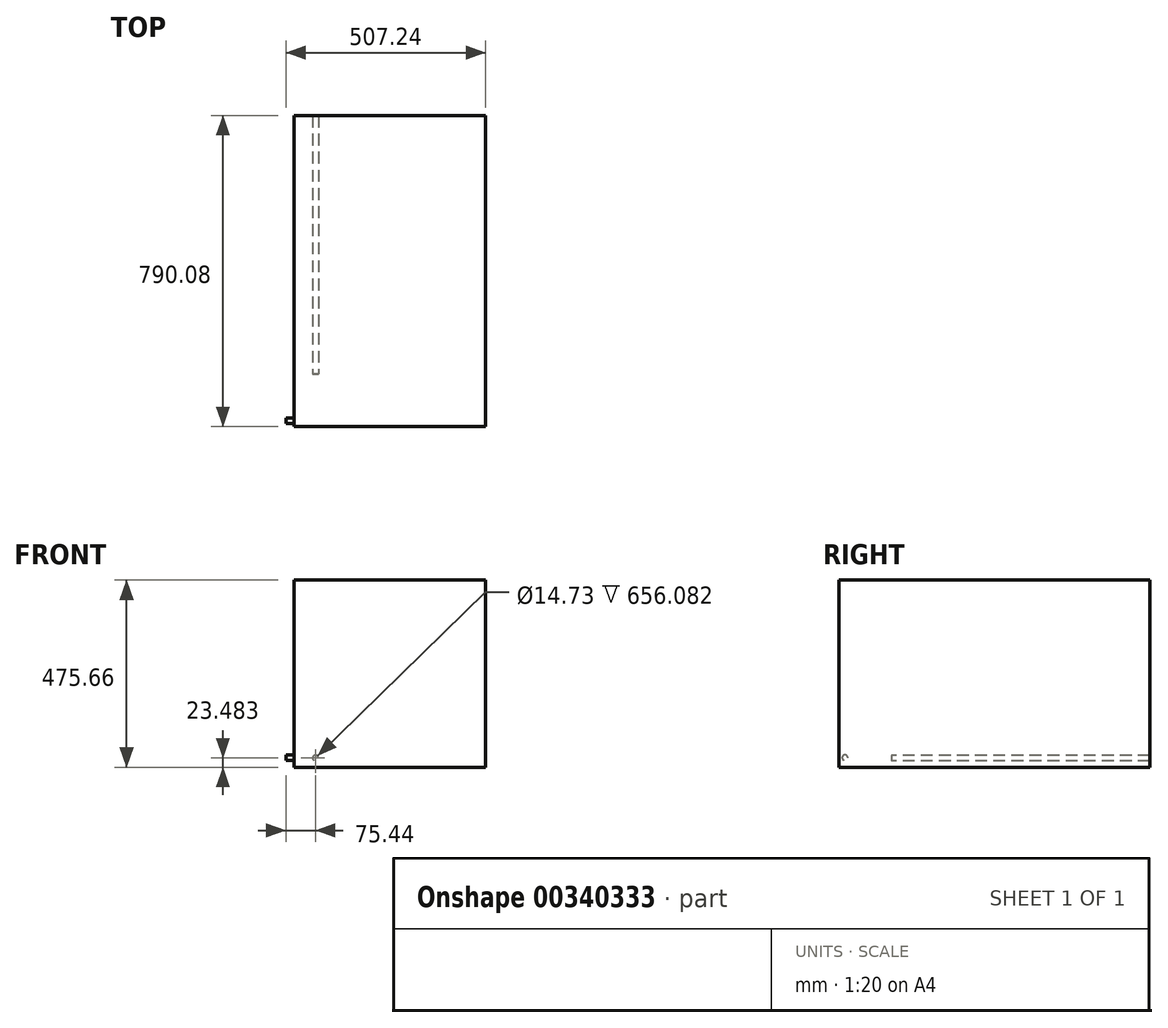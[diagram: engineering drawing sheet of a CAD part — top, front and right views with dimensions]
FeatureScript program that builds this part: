
annotation { "Feature Type Name" : "Feature", "Feature Type Description" : "" }
export const myFeature = defineFeature(function(context is Context, id is Id, definition is map)
    precondition{}
    {
        {
            var Q0;
            Q0=qCreatedBy(makeId("Right.planeOp"),FACE);
            var sketch = newSketch(context, id + "F0", { "sketchPlane" : qUnion([Q0])});
            skLineSegment(sketch, "E0", {"start": v(-46.44, -18.34) * mm, "end": v(36, -18.34) * mm});
            skLineSegment(sketch, "E1", {"start": v(-46.44, 25.52) * mm, "end": v(36, 25.52) * mm});
            skLineSegment(sketch, "E2", {"start": v(-46.44, 25.52) * mm, "end": v(-46.44, -18.34) * mm});
            skLineSegment(sketch, "E3", {"start": v(36, 25.52) * mm, "end": v(36, -18.34) * mm});
            skSolve(sketch);
        }
        {
            var Q0;
            Q0 = qSketchRegion(id + "F0", true);
            extrude(context, id + "F1", {"entities" : qUnion([Q0]), "depth" : 431.8 * mm});
        }
        {
            var Q0;
            Q0=makeQuery(id+"F1.opExtrude","CAP_FACE",FACE,{"disambiguationData":[OSD([sQuery(id+"F0.wireOp",EDGE,"E0"),sQuery(id+"F0.wireOp",EDGE,"E1"),sQuery(id+"F0.wireOp",EDGE,"E2"),sQuery(id+"F0.wireOp",EDGE,"E3")])],"isStart":true});
            extrude(context, id + "F2", {"entities" : qUnion([Q0]), "operationType" : NewBodyOperationType.ADD, "depth" : 54.86 * mm});
        }
        {
            var Q0;
            Q0=makeQuery(id+"F2.opExtrude","CAP_FACE",FACE,{"disambiguationData":[OSD([sQuery(id+"F0.wireOp",EDGE,"E0"),sQuery(id+"F0.wireOp",EDGE,"E1"),sQuery(id+"F0.wireOp",EDGE,"E2"),sQuery(id+"F0.wireOp",EDGE,"E3")])],"isStart":false});
            var sketch = newSketch(context, id + "F3", { "sketchPlane" : qUnion([Q0])});
            skCircle(sketch, "E4", {"center": v(31.25, 5.96) * mm, "radius": 7.09 * mm});
            skSolve(sketch);
        }
        {
            var Q0;
            Q0=makeQuery(id+"F3.imprint","IMPRINT",FACE,{"disambiguationData":[TD([[makeQuery(id+"F3.imprint","IMPRINT",EDGE,{"derivedFrom":sQuery(id+"F3.wireOp",EDGE,"E4")}),1.0]])]});
            extrude(context, id + "F4", {"entities" : qUnion([Q0]), "operationType" : NewBodyOperationType.ADD, "depth" : 20.57 * mm});
        }
        {
            var Q0;
            {var subQ0=sQuery(id+"F0.wireOp",EDGE,"E3");Q0=makeQuery(id+"F2.boolean.opBoolean","MERGE",FACE,{"derivedFrom":[makeQuery(id+"F1.opExtrude","SWEPT_FACE",FACE,{"disambiguationData":[OSD([subQ0])]}),makeQuery(id+"F2.opExtrude","SWEPT_FACE",FACE,{"disambiguationData":[OSD([subQ0])]})]});}
            var sketch = newSketch(context, id + "F5", { "sketchPlane" : qUnion([Q0])});
            skCircle(sketch, "E5", {"center": v(0, 5.14) * mm, "radius": 7.36 * mm});
            skSolve(sketch);
        }
        {
            var Q0;
            Q0=makeQuery(id+"F5.imprint","IMPRINT",FACE,{"disambiguationData":[TD([[makeQuery(id+"F5.imprint","IMPRINT",EDGE,{"derivedFrom":sQuery(id+"F5.wireOp",EDGE,"E5")}),1.0]])]});
            extrude(context, id + "F6", {"entities" : qUnion([Q0]), "operationType" : NewBodyOperationType.ADD, "depth" : 14.48 * mm});
        }
        {
            var Q0;
            {var subQ0=sQuery(id+"F0.wireOp",EDGE,"E3");Q0=makeQuery(id+"F2.boolean.opBoolean","MERGE",FACE,{"derivedFrom":[makeQuery(id+"F1.opExtrude","SWEPT_FACE",FACE,{"disambiguationData":[OSD([subQ0])]}),makeQuery(id+"F2.opExtrude","SWEPT_FACE",FACE,{"disambiguationData":[OSD([subQ0])]})]});}
            extrude(context, id + "F7", {"entities" : qUnion([Q0]), "operationType" : NewBodyOperationType.ADD, "depth" : 34.54 * mm});
        }
        {
            var Q0;
            Q0=makeQuery(id+"F6.opExtrude","CAP_FACE",FACE,{"disambiguationData":[OSD([sQuery(id+"F5.wireOp",EDGE,"E5")])],"isStart":false});
            extrude(context, id + "F8", {"entities" : qUnion([Q0]), "operationType" : NewBodyOperationType.ADD, "depth" : 37.08 * mm});
        }
        {
            var Q0;
            Q0=makeQuery(id+"F7.opExtrude","CAP_FACE",FACE,{"disambiguationData":[OSD([sQuery(id+"F0.wireOp",EDGE,"E3")])],"isStart":false});
            extrude(context, id + "F9", {"entities" : qUnion([Q0]), "operationType" : NewBodyOperationType.ADD, "depth" : 673.1 * mm});
        }
        {
            var Q0;
            {var subQ0=sQuery(id+"F0.wireOp",EDGE,"E3");var subQ1=sQuery(id+"F0.wireOp",EDGE,"E1");Q0=makeQuery(id+"F9.boolean.opBoolean","MERGE",FACE,{"derivedFrom":[makeQuery(id+"F7.boolean.opBoolean","MERGE",FACE,{"derivedFrom":[makeQuery(id+"F2.boolean.opBoolean","MERGE",FACE,{"derivedFrom":[makeQuery(id+"F1.opExtrude","SWEPT_FACE",FACE,{"disambiguationData":[OSD([subQ1])]}),makeQuery(id+"F2.opExtrude","SWEPT_FACE",FACE,{"disambiguationData":[OSD([subQ1])]})]}),makeQuery(id+"F7.opExtrude","SWEPT_FACE",FACE,{"disambiguationData":[OSD([subQ1,subQ0])]})]}),makeQuery(id+"F9.opExtrude","SWEPT_FACE",FACE,{"disambiguationData":[OSD([subQ1,subQ0])]})]});}
            extrude(context, id + "F10", {"entities" : qUnion([Q0]), "operationType" : NewBodyOperationType.ADD, "depth" : 431.8 * mm});
        }
    });
